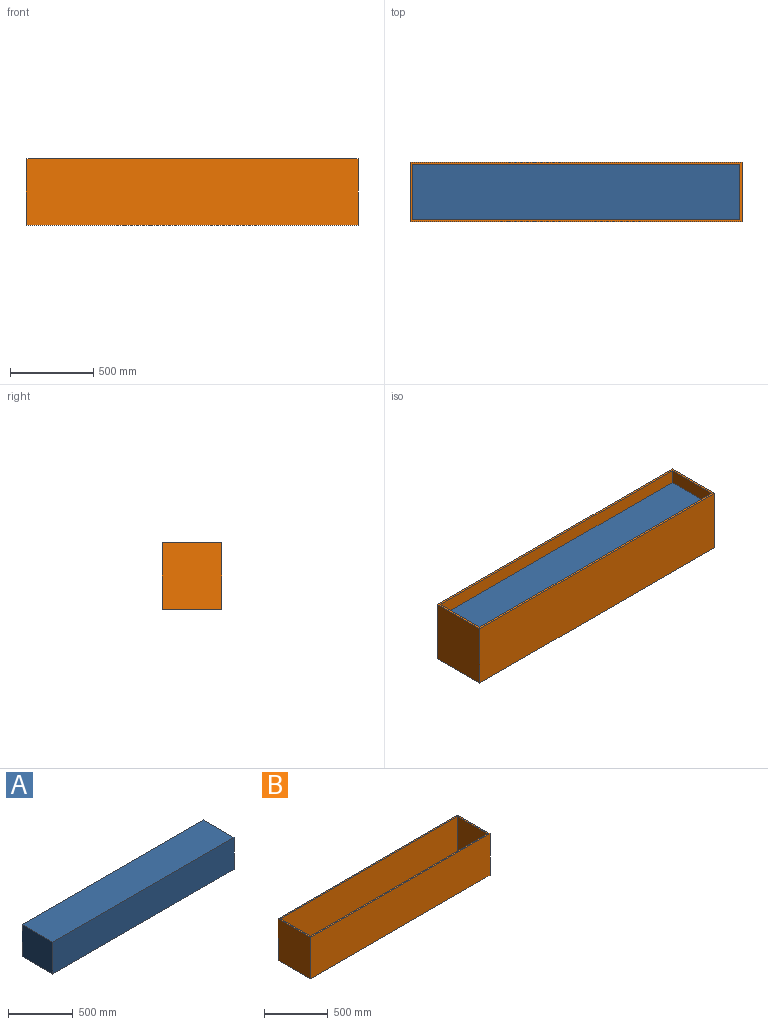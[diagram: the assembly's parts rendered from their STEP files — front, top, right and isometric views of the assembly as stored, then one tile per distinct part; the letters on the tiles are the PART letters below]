
ASSEMBLY  parts=2 mates=1
PART A: 6 faces, bbox 1974.6x334.6x300 mm
  f0: plane 334.6x300mm, normal (1,0,0), area 100380mm2, adj f1,f3,f4,f5
  f1: plane 1974.6x300mm, normal (0,1,0), area 592380mm2, adj f0,f2,f4,f5
  f2: plane 334.6x300mm, normal (-1,0,0), area 100380mm2, adj f1,f3,f4,f5
  f3: plane 1974.6x300mm, normal (0,-1,0), area 592380mm2, adj f0,f2,f4,f5
  f4: plane 1974.6x334.6mm, normal (0,0,1), area 660701.2mm2, adj f0,f1,f2,f3
  f5: plane 1974.6x334.6mm, normal (0,0,-1), area 660701.2mm2, adj f0,f1,f2,f3
PART B: 11 faces, bbox 2000x360x400 mm
  f0: plane 400x360mm, normal (-1,0,0), area 144000mm2, adj f1,f7,f8,f9
  f1: plane 2000x400mm, normal (0,-1,0), area 800000mm2, adj f0,f2,f8,f9
  f2: plane 400x360mm, normal (1,0,0), area 144000mm2, adj f1,f7,f8,f9
  f3: plane 387.3x334.6mm, normal (1,0,0), area 129590.6mm2, adj f4,f6,f8,f10
  f4: plane 1974.6x387.3mm, normal (0,-1,0), area 764762.6mm2, adj f3,f5,f8,f10
  f5: plane 387.3x334.6mm, normal (-1,0,0), area 129590.6mm2, adj f4,f6,f8,f10
  f6: plane 1974.6x387.3mm, normal (0,1,0), area 764762.6mm2, adj f3,f5,f8,f10
  f7: plane 2000x400mm, normal (0,1,0), area 800000mm2, adj f0,f2,f8,f9
  f8: plane 2000x360mm, normal (0,0,1), area 59298.8mm2, adj f0,f1,f2,f3,f4,f5,f6,f7
  f9: plane 2000x360mm, normal (0,0,-1), area 720000mm2, adj f0,f1,f2,f7
  f10: plane 1974.6x334.6mm, normal (0,0,1), area 660701.2mm2, adj f3,f4,f5,f6
PLACE A t=(-204.31,214.28,348.36)mm
PLACE B t=(-204.31,214.28,335.66)mm
MATE fastened B.f10 <-> A.f5  axis (0,0,1) through (-1191.61,46.98,348.36)mm
